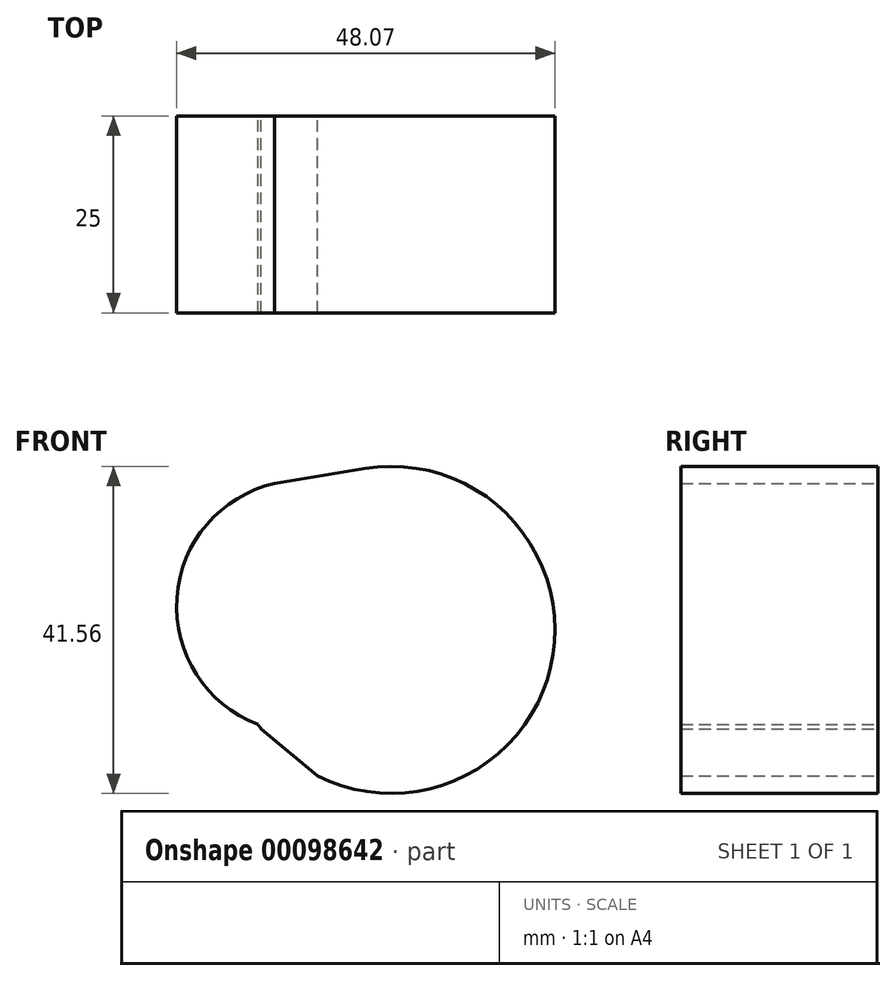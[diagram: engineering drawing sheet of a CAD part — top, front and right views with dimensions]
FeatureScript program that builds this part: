
annotation { "Feature Type Name" : "Feature", "Feature Type Description" : "" }
export const myFeature = defineFeature(function(context is Context, id is Id, definition is map)
    precondition{}
    {
        {
            var Q0;
            Q0=qCreatedBy(makeId("Front.planeOp"),FACE);
            var sketch = newSketch(context, id + "F0", { "sketchPlane" : qUnion([Q0])});
            skCircle(sketch, "E0", {"center": v(0, 0) * mm, "radius": 20.78 * mm});
            skCircle(sketch, "E1", {"center": v(-11.27, 2.97) * mm, "radius": 16.02 * mm});
            skLineSegment(sketch, "E2", {"start": v(-14.82, 18.6) * mm, "end": v(0, 21.06) * mm});
            skLineSegment(sketch, "E3", {"start": v(-24.7, -5.77) * mm, "end": v(-9.36, -18.55) * mm});
            skSolve(sketch);
        }
        {
            var Q0;
            {var subQ0=sQuery(id+"F0.wireOp",EDGE,"E1");var subQ1=sQuery(id+"F0.wireOp",EDGE,"E0");var subQ2=makeQuery(id+"F0.imprint","INTERSECT",VERTEX,{"disambiguationData":[OD(0.0)],"derivedFrom":[subQ1,subQ0]});Q0=makeQuery(id+"F0.imprint","IMPRINT",FACE,{"disambiguationData":[TD([[makeQuery(id+"F0.imprint","IMPRINT",EDGE,{"disambiguationData":[TD([[subQ2,-1.0]])],"derivedFrom":subQ1}),1.0]])]});}
            var Q1;
            {var subQ1=sQuery(id+"F0.wireOp",EDGE,"E0");var subQ6=makeQuery(id+"F0.imprint","INTERSECT",VERTEX,{"derivedFrom":[subQ1,sQuery(id+"F0.wireOp",EDGE,"E2")]});Q1=makeQuery(id+"F0.imprint","IMPRINT",FACE,{"disambiguationData":[TD([[makeQuery(id+"F0.imprint","IMPRINT",EDGE,{"disambiguationData":[TD([[subQ6,-1.0]])],"derivedFrom":subQ1}),1.0]])]});}
            var Q2;
            {var subQ0=sQuery(id+"F0.wireOp",EDGE,"E2");var subQ1=sQuery(id+"F0.wireOp",EDGE,"E0");var subQ2=makeQuery(id+"F0.imprint","INTERSECT",VERTEX,{"derivedFrom":[subQ1,subQ0]});Q2=makeQuery(id+"F0.imprint","IMPRINT",FACE,{"disambiguationData":[TD([[makeQuery(id+"F0.imprint","IMPRINT",EDGE,{"disambiguationData":[TD([[subQ2,-1.0]])],"derivedFrom":subQ1}),-1.0]])]});}
            var Q3;
            {var subQ0=sQuery(id+"F0.wireOp",EDGE,"E3");var subQ1=sQuery(id+"F0.wireOp",EDGE,"E1");var subQ2=makeQuery(id+"F0.imprint","INTERSECT",VERTEX,{"disambiguationData":[OD(0.0)],"derivedFrom":[subQ1,subQ0]});Q3=makeQuery(id+"F0.imprint","IMPRINT",FACE,{"disambiguationData":[TD([[makeQuery(id+"F0.imprint","IMPRINT",EDGE,{"disambiguationData":[TD([[subQ2,-1.0]])],"derivedFrom":subQ1}),1.0]])]});}
            var Q4;
            {var subQ1=sQuery(id+"F0.wireOp",EDGE,"E1");var subQ3=sQuery(id+"F0.wireOp",EDGE,"E0");var subQ9=makeQuery(id+"F0.imprint","INTERSECT",VERTEX,{"disambiguationData":[OD(0.0)],"derivedFrom":[subQ3,subQ1]});Q4=makeQuery(id+"F0.imprint","IMPRINT",FACE,{"disambiguationData":[TD([[makeQuery(id+"F0.imprint","IMPRINT",EDGE,{"disambiguationData":[TD([[subQ9,-1.0]])],"derivedFrom":subQ3}),-1.0]])]});}
            var Q5;
            {var subQ0=sQuery(id+"F0.wireOp",EDGE,"E3");var subQ1=sQuery(id+"F0.wireOp",EDGE,"E0");var subQ2=makeQuery(id+"F0.imprint","INTERSECT",VERTEX,{"disambiguationData":[OD(0.0)],"derivedFrom":[subQ1,subQ0]});Q5=makeQuery(id+"F0.imprint","IMPRINT",FACE,{"disambiguationData":[TD([[makeQuery(id+"F0.imprint","IMPRINT",EDGE,{"disambiguationData":[TD([[subQ2,1.0]])],"derivedFrom":subQ1}),1.0]])]});}
            extrude(context, id + "F1", {"entities" : qUnion([Q0, Q1, Q2, Q3, Q4, Q5]), "depth" : 25 * mm});
        }
    });
